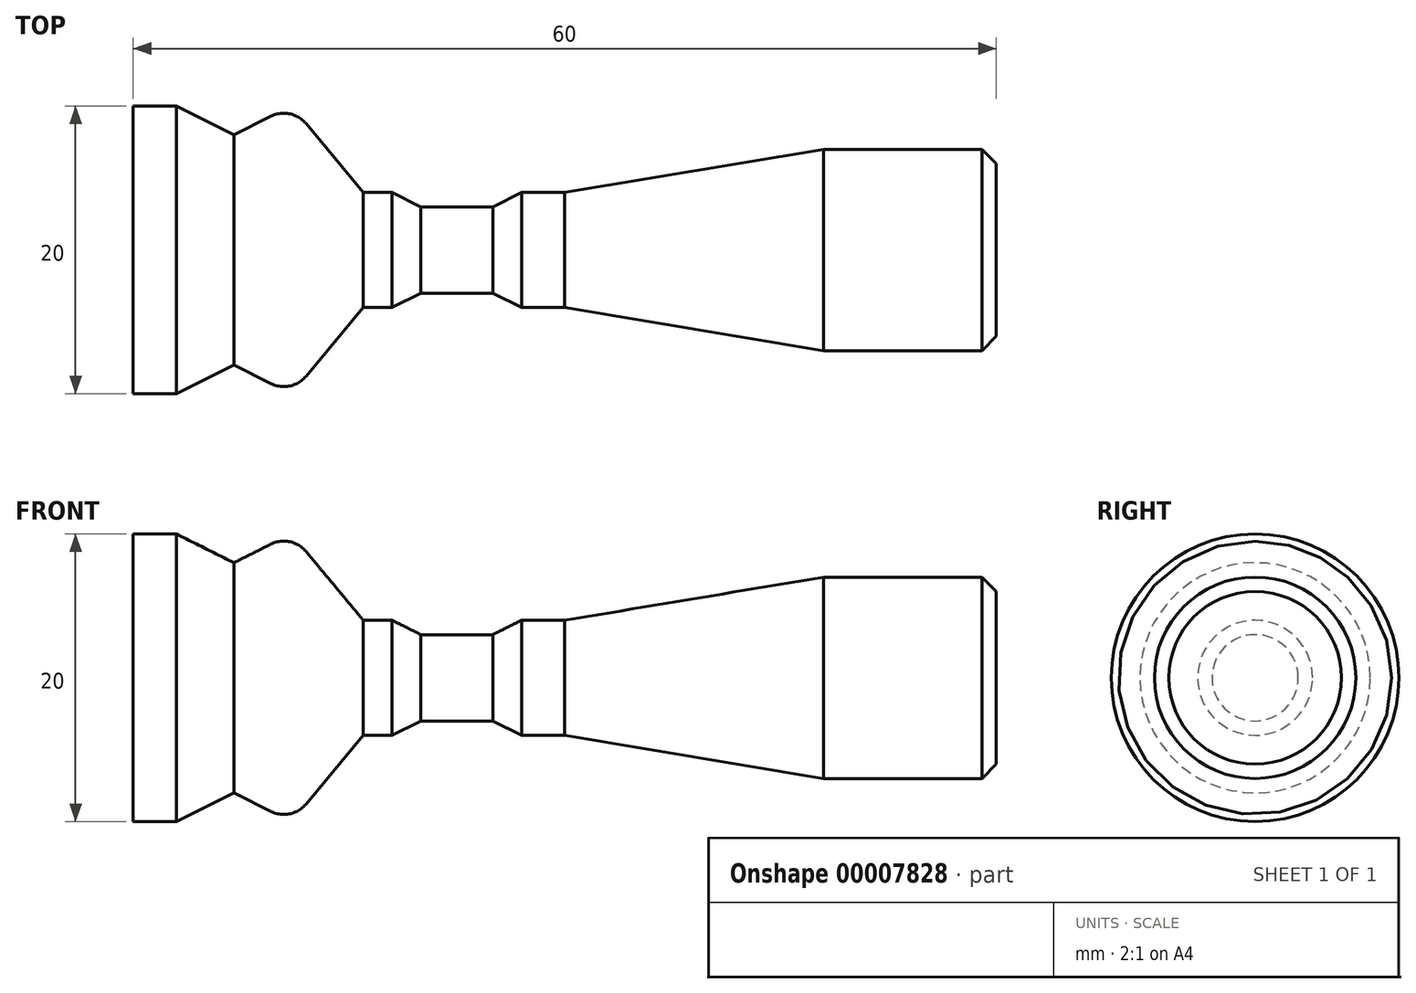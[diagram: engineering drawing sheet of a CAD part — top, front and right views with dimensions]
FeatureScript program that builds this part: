
annotation { "Feature Type Name" : "Feature", "Feature Type Description" : "" }
export const myFeature = defineFeature(function(context is Context, id is Id, definition is map)
    precondition{}
    {
        {
            var Q0;
            Q0=qCreatedBy(makeId("Front.planeOp"),FACE);
            var sketch = newSketch(context, id + "F0", { "sketchPlane" : qUnion([Q0])});
            skLineSegment(sketch, "E0", {"start": v(-44.83, 0) * mm, "end": v(32.17, 0) * mm});
            skLineSegment(sketch, "E1", {"start": v(27.17, 0) * mm, "end": v(27.17, -7) * mm});
            skLineSegment(sketch, "E2", {"start": v(27.17, -7) * mm, "end": v(15.17, -7) * mm});
            skLineSegment(sketch, "E3", {"start": v(15.17, -7) * mm, "end": v(-2.83, -4) * mm});
            skLineSegment(sketch, "E4", {"start": v(-2.83, -4) * mm, "end": v(-5.83, -4) * mm});
            skLineSegment(sketch, "E5", {"start": v(-5.83, -4) * mm, "end": v(-7.83, -3) * mm});
            skLineSegment(sketch, "E6", {"start": v(-7.83, -3) * mm, "end": v(-12.83, -3) * mm});
            skLineSegment(sketch, "E7", {"start": v(-12.83, -3) * mm, "end": v(-14.83, -4) * mm});
            skLineSegment(sketch, "E8", {"start": v(-14.83, -4) * mm, "end": v(-16.83, -4) * mm});
            skLineSegment(sketch, "E9", {"start": v(-16.83, -4) * mm, "end": v(-21.83, -10) * mm});
            skLineSegment(sketch, "E10", {"start": v(-21.83, -10) * mm, "end": v(-25.83, -8) * mm});
            skLineSegment(sketch, "E11", {"start": v(-29.83, -10) * mm, "end": v(-32.83, -10) * mm});
            skLineSegment(sketch, "E12", {"start": v(-29.83, -10) * mm, "end": v(-25.83, -8) * mm});
            skLineSegment(sketch, "E13", {"start": v(-32.83, -10) * mm, "end": v(-32.83, 0) * mm});
            skSolve(sketch);
        }
        {
            var Q0;
            {var subQ1=sQuery(id+"F0.wireOp",EDGE,"E1");Q0=makeQuery(id+"F0.imprint","IMPRINT",FACE,{"disambiguationData":[TD([[makeQuery(id+"F0.imprint","IMPRINT",EDGE,{"derivedFrom":subQ1}),-1.0]])]});}
            var Q1;
            Q1=sQuery(id+"F0.wireOp",EDGE,"E0");
            revolve(context, id + "F1", {"entities" : qUnion([Q0]), "axis" : qUnion([Q1]), "revolveType" : RevolveType.FULL});
        }
        {
            var Q0;
            Q0=makeQuery(id+"F1.opRevolve","SWEPT_EDGE",EDGE,{"disambiguationData":[OSD([sQuery(id+"F0.wireOp",EDGE,"E1"),sQuery(id+"F0.wireOp",EDGE,"E2")])]});
            chamfer(context, id + "F2", {"entities" : qUnion([Q0]), "width" : 1 * mm});
        }
        {
            var Q0;
            Q0=makeQuery(id+"F1.opRevolve","SWEPT_EDGE",EDGE,{"disambiguationData":[OSD([sQuery(id+"F0.wireOp",EDGE,"E9"),sQuery(id+"F0.wireOp",EDGE,"E10")])]});
            fillet(context, id + "F3", {"entities" : qUnion([Q0]), "radius" : 2 * mm, "allowEdgeOverflow" : false});
        }
    });
